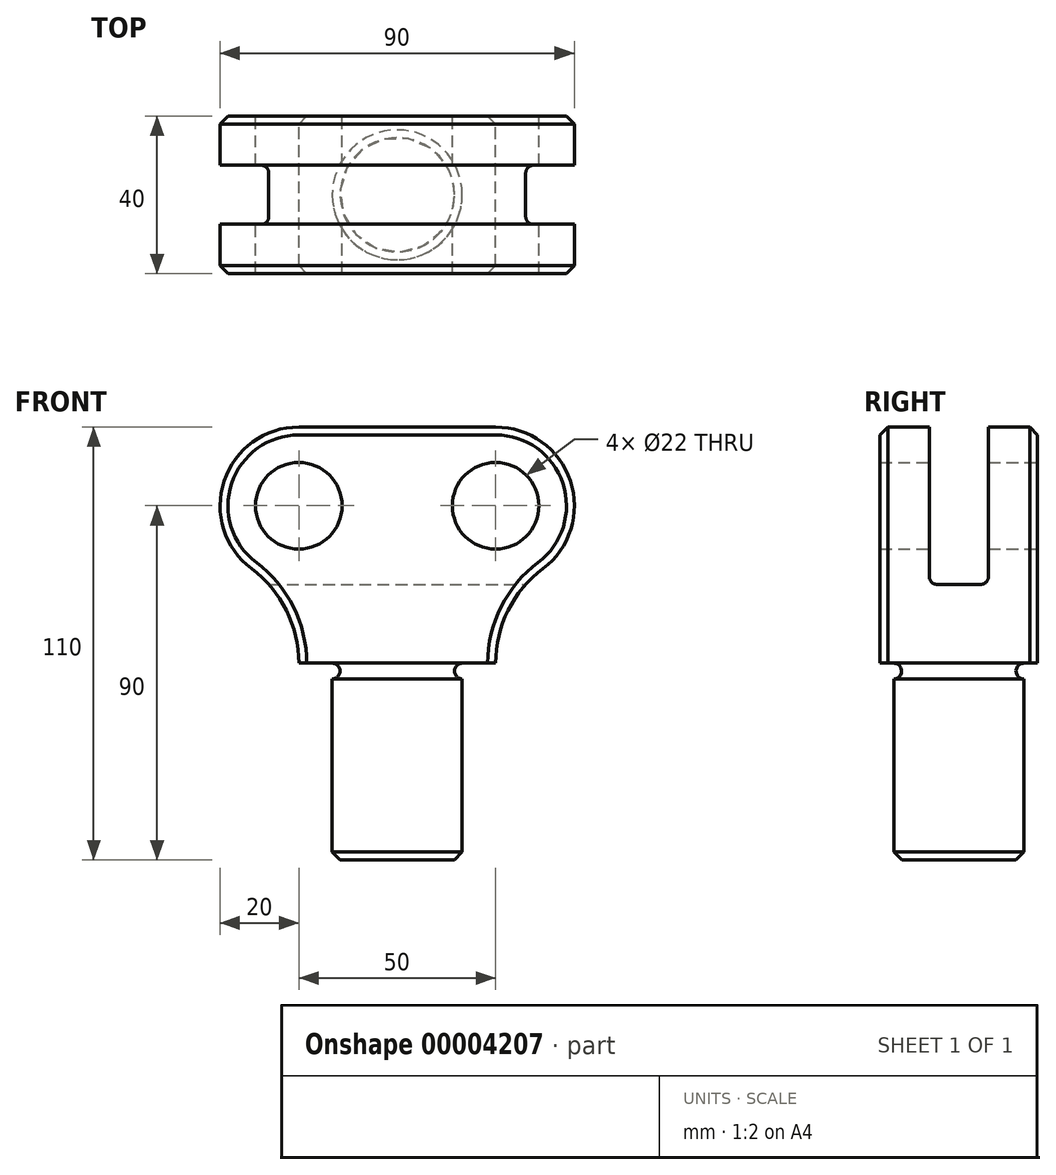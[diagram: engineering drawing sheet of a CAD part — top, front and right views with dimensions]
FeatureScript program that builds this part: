
annotation { "Feature Type Name" : "Feature", "Feature Type Description" : "" }
export const myFeature = defineFeature(function(context is Context, id is Id, definition is map)
    precondition{}
    {
        {
            var Q0;
            Q0=qCreatedBy(makeId("Front.planeOp"),FACE);
            var sketch = newSketch(context, id + "F0", { "sketchPlane" : qUnion([Q0])});
            skLineSegment(sketch, "E0", {"start": v(-25, 0) * mm, "end": v(25, 0) * mm, "construction": true});
            skCircle(sketch, "E1", {"center": v(-25, 0) * mm, "radius": 11 * mm});
            skCircle(sketch, "E2", {"center": v(25, 0) * mm, "radius": 11 * mm});
            skLineSegment(sketch, "E3", {"start": v(25, 20) * mm, "end": v(-25, 20) * mm});
            skLineSegment(sketch, "E4", {"start": v(-25, -20) * mm, "end": v(25, -20) * mm});
            skArc(sketch, "E5", {"start": v(-25, 20) * mm, "mid": v(-45, 0) * mm, "end": v(-25, -20) * mm});
            skArc(sketch, "E6", {"start": v(25, 20) * mm, "mid": v(45, 0) * mm, "end": v(25, -20) * mm});
            skPoint(sketch, "E7", {"position": v(0, 0) * mm});
            skLineSegment(sketch, "E8", {"start": v(-25, -20) * mm, "end": v(-25, -40) * mm});
            skLineSegment(sketch, "E9", {"start": v(-25, -40) * mm, "end": v(25, -40) * mm});
            skLineSegment(sketch, "E10", {"start": v(25, -40) * mm, "end": v(25, -20) * mm});
            skSolve(sketch);
        }
        {
            var Q0;
            Q0 = qSketchRegion(id + "F0", true);
            extrude(context, id + "F1", {"entities" : qUnion([Q0]), "endBound" : BoundingType.SYMMETRIC, "depth" : 40 * mm});
        }
        {
            var Q0;
            Q0=makeQuery(id+"F1.opExtrude","SWEPT_EDGE",EDGE,{"disambiguationData":[OSD([sQuery(id+"F0.wireOp",EDGE,"E4"),sQuery(id+"F0.wireOp",EDGE,"E6"),sQuery(id+"F0.wireOp",EDGE,"E10")])]});
            var Q1;
            Q1=makeQuery(id+"F1.opExtrude","SWEPT_EDGE",EDGE,{"disambiguationData":[OSD([sQuery(id+"F0.wireOp",EDGE,"E4"),sQuery(id+"F0.wireOp",EDGE,"E5"),sQuery(id+"F0.wireOp",EDGE,"E8")])]});
            fillet(context, id + "F2", {"entities" : qUnion([Q0, Q1]), "radius" : 30 * mm, "tangentPropagation" : true, "allowEdgeOverflow" : false});
        }
        {
            var Q0;
            Q0=makeQuery(id+"F1.opExtrude","SWEPT_FACE",FACE,{"disambiguationData":[OSD([sQuery(id+"F0.wireOp",EDGE,"E9")])]});
            var sketch = newSketch(context, id + "F3", { "sketchPlane" : qUnion([Q0])});
            skCircle(sketch, "E11", {"center": v(0, 0) * mm, "radius": 16.5 * mm});
            skSolve(sketch);
        }
        {
            var Q0;
            Q0 = qSketchRegion(id + "F3", true);
            extrude(context, id + "F4", {"entities" : qUnion([Q0]), "operationType" : NewBodyOperationType.ADD, "depth" : 50 * mm});
        }
        {
            var Q0;
            Q0=makeQuery(id+"F1.opExtrude","SWEPT_FACE",FACE,{"disambiguationData":[OSD([sQuery(id+"F0.wireOp",EDGE,"E3")])]});
            var sketch = newSketch(context, id + "F5", { "sketchPlane" : qUnion([Q0])});
            skLineSegment(sketch, "E12.rect.bottom", {"start": v(-57.21, -7.5) * mm, "end": v(57.21, -7.5) * mm});
            skLineSegment(sketch, "E12.rect.top", {"start": v(-57.21, 7.5) * mm, "end": v(57.21, 7.5) * mm});
            skLineSegment(sketch, "E12.rect.left", {"start": v(-57.21, -7.5) * mm, "end": v(-57.21, 7.5) * mm});
            skLineSegment(sketch, "E12.rect.right", {"start": v(57.21, -7.5) * mm, "end": v(57.21, 7.5) * mm});
            skPoint(sketch, "E12.rect.middle", {"position": v(0, 0) * mm});
            skSolve(sketch);
        }
        {
            var Q0;
            Q0 = qSketchRegion(id + "F5", true);
            extrude(context, id + "F6", {"entities" : qUnion([Q0]), "operationType" : NewBodyOperationType.REMOVE, "oppositeDirection" : true, "depth" : 40 * mm});
        }
        {
            var Q0;
            Q0=makeQuery(id+"F6.boolean.opBoolean","COPY",EDGE,{"derivedFrom":makeQuery(id+"F6.opExtrude","CAP_EDGE",EDGE,{"disambiguationData":[OSD([sQuery(id+"F5.wireOp",EDGE,"E12.rect.top")])],"isStart":false})});
            var Q1;
            Q1=makeQuery(id+"F6.boolean.opBoolean","COPY",EDGE,{"derivedFrom":makeQuery(id+"F6.opExtrude","CAP_EDGE",EDGE,{"disambiguationData":[OSD([sQuery(id+"F5.wireOp",EDGE,"E12.rect.bottom")])],"isStart":false})});
            fillet(context, id + "F7", {"entities" : qUnion([Q0, Q1]), "radius" : 2 * mm, "tangentPropagation" : true, "allowEdgeOverflow" : false});
        }
        {
            var Q0;
            {var subQ0=sQuery(id+"F0.wireOp",EDGE,"E6");var subQ1=sQuery(id+"F0.wireOp",EDGE,"E10");Q0=makeQuery(id+"F2.opFillet","BLEND_EDGE",EDGE,{"blendedFrom":[makeQuery(id+"F1.opExtrude","SWEPT_EDGE",EDGE,{"disambiguationData":[OSD([sQuery(id+"F0.wireOp",EDGE,"E4"),subQ0,subQ1])]}),makeQuery(id+"F1.opExtrude","CAP_FACE",FACE,{"disambiguationData":[OSD([sQuery(id+"F0.wireOp",EDGE,"E1"),sQuery(id+"F0.wireOp",EDGE,"E2"),sQuery(id+"F0.wireOp",EDGE,"E3"),sQuery(id+"F0.wireOp",EDGE,"E5"),subQ0,sQuery(id+"F0.wireOp",EDGE,"E8"),sQuery(id+"F0.wireOp",EDGE,"E9"),subQ1])],"isStart":false})],"blendedInto":[makeQuery(id+"F1.opExtrude","CAP_FACE",FACE,{"disambiguationData":[OSD([sQuery(id+"F0.wireOp",EDGE,"E1"),sQuery(id+"F0.wireOp",EDGE,"E2"),sQuery(id+"F0.wireOp",EDGE,"E3"),sQuery(id+"F0.wireOp",EDGE,"E5"),subQ0,sQuery(id+"F0.wireOp",EDGE,"E8"),sQuery(id+"F0.wireOp",EDGE,"E9"),subQ1])],"isStart":false})]});}
            var Q1;
            {var subQ0=sQuery(id+"F0.wireOp",EDGE,"E6");var subQ1=sQuery(id+"F0.wireOp",EDGE,"E10");Q1=makeQuery(id+"F2.opFillet","BLEND_EDGE",EDGE,{"blendedFrom":[makeQuery(id+"F1.opExtrude","SWEPT_EDGE",EDGE,{"disambiguationData":[OSD([sQuery(id+"F0.wireOp",EDGE,"E4"),subQ0,subQ1])]}),makeQuery(id+"F1.opExtrude","CAP_FACE",FACE,{"disambiguationData":[OSD([sQuery(id+"F0.wireOp",EDGE,"E1"),sQuery(id+"F0.wireOp",EDGE,"E2"),sQuery(id+"F0.wireOp",EDGE,"E3"),sQuery(id+"F0.wireOp",EDGE,"E5"),subQ0,sQuery(id+"F0.wireOp",EDGE,"E8"),sQuery(id+"F0.wireOp",EDGE,"E9"),subQ1])],"isStart":true})],"blendedInto":[makeQuery(id+"F1.opExtrude","CAP_FACE",FACE,{"disambiguationData":[OSD([sQuery(id+"F0.wireOp",EDGE,"E1"),sQuery(id+"F0.wireOp",EDGE,"E2"),sQuery(id+"F0.wireOp",EDGE,"E3"),sQuery(id+"F0.wireOp",EDGE,"E5"),subQ0,sQuery(id+"F0.wireOp",EDGE,"E8"),sQuery(id+"F0.wireOp",EDGE,"E9"),subQ1])],"isStart":true})]});}
            var Q2;
            Q2=makeQuery(id+"F4.opExtrude","CAP_EDGE",EDGE,{"disambiguationData":[OSD([sQuery(id+"F3.wireOp",EDGE,"E11")])],"isStart":false});
            chamfer(context, id + "F8", {"entities" : qUnion([Q0, Q1, Q2]), "width" : 2 * mm, "tangentPropagation" : true});
        }
        {
            var Q0;
            Q0=qCreatedBy(makeId("Front.planeOp"),FACE);
            var sketch = newSketch(context, id + "F9", { "sketchPlane" : qUnion([Q0])});
            skCircle(sketch, "E13", {"center": v(16.53, -42) * mm, "radius": 2 * mm});
            skLineSegment(sketch, "E14", {"start": v(16.53, -48.32) * mm, "end": v(16.53, -41.03) * mm, "construction": true});
            skSolve(sketch);
        }
        {
            var Q0;
            Q0 = qSketchRegion(id + "F9", true);
            var Q1;
            {var subQ0=sQuery(id+"F3.wireOp",EDGE,"E11");Q1=makeQuery(id+"F8.opChamfer","BLEND_EDGE",EDGE,{"blendedFrom":[makeQuery(id+"F4.opExtrude","CAP_EDGE",EDGE,{"disambiguationData":[OSD([subQ0])],"isStart":false}),makeQuery(id+"F4.opExtrude","SWEPT_FACE",FACE,{"disambiguationData":[OSD([subQ0])]})],"blendedInto":[makeQuery(id+"F4.opExtrude","SWEPT_FACE",FACE,{"disambiguationData":[OSD([subQ0])]})]});}
            revolve(context, id + "F10", {"operationType" : NewBodyOperationType.REMOVE, "entities" : qUnion([Q0]), "axis" : qUnion([Q1]), "revolveType" : RevolveType.FULL});
        }
    });
